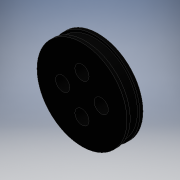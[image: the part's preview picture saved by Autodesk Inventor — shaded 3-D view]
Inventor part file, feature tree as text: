
AUTODESK INVENTOR PART (.ipt)
format: ipt  version: 2016 (Build 200138000, 138)  size: 125,952 bytes
history: native  units: mm
features: sketch x4, extrude x3, hole x1
ambient origin geometry x8: Origin, YZ Plane, XZ Plane, XY Plane, X Axis, Y Axis, Z Axis, Center Point
bodies: Solid1 (feature_tree)
feature tree (8):
  extrude  "Extrusion1"  Depth=1.0mm TaperAngle=0.0deg
  extrude  "Extrusion2"  Depth=3.0mm TaperAngle=0.0deg
  extrude  "Extrusion3"  Depth=1.0mm TaperAngle=0.0deg
  hole  "Hole1"  [1 undecoded]
  sketch  "Sketch1"  dims[d0=28.0mm d1=1.0mm d2=0.0mm]
  sketch  "Sketch2"  dims[d3=26.5mm d4=3.0mm d5=0.0mm]
  sketch  "Sketch3"  dims[d6=28.0mm d7=1.0mm d8=0.0mm]
  sketch  "Sketch4"  dims[d9=4.4mm d10=6.0mm d11=4.4mm d12=12.0mm d13=4.4mm d14=6.0mm d15=4.4mm d16=6.0mm d17=4.4mm d18=6.0mm d19=4.0mm d20=2.0mm d21=90.0deg d22=8.0mm d23=20.594885mm]
note: 1 required parameter value undecoded (feature->parameter linkage not recoverable at this tier; creation-order binding heuristic only, values carry confidence <= 0.55)
